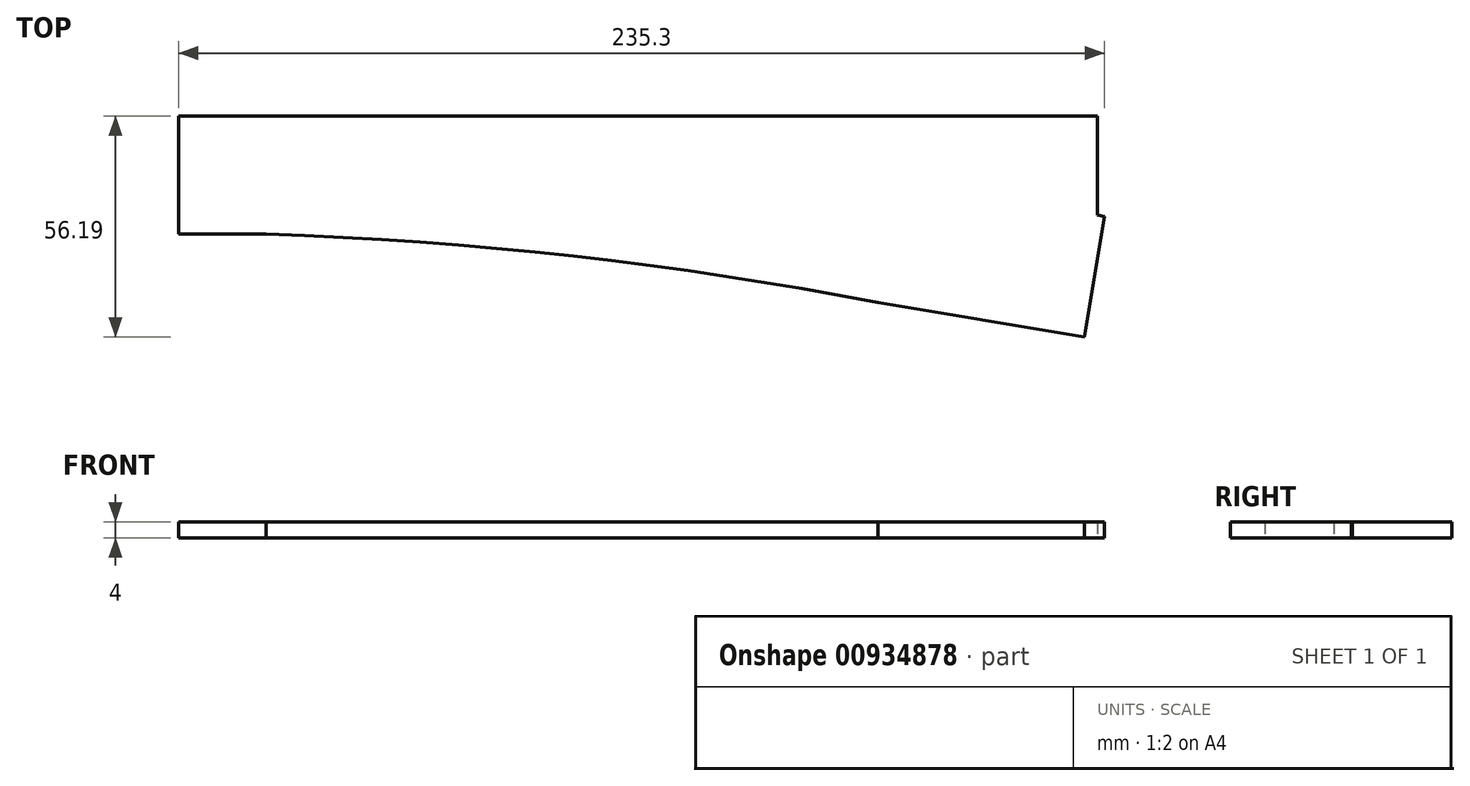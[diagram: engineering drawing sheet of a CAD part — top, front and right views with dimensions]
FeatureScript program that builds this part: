
annotation { "Feature Type Name" : "Feature", "Feature Type Description" : "" }
export const myFeature = defineFeature(function(context is Context, id is Id, definition is map)
    precondition{}
    {
        {
            var Q0;
            Q0=qCreatedBy(makeId("Top.planeOp"),FACE);
            var sketch = newSketch(context, id + "F0", { "sketchPlane" : qUnion([Q0])});
            skPoint(sketch, "E0.startSnap0", {"position": v(97.75, -3.18) * mm});
            skLineSegment(sketch, "E1.bottom", {"start": v(-138.74, -10.87) * mm, "end": v(94.76, -10.87) * mm});
            skLineSegment(sketch, "E1.top", {"start": v(-138.74, -40.87) * mm, "end": v(-116.46, -40.87) * mm});
            skLineSegment(sketch, "E1.left", {"start": v(-138.74, -10.87) * mm, "end": v(-138.74, -40.87) * mm});
            skLineSegment(sketch, "E1.right", {"start": v(94.76, -10.87) * mm, "end": v(94.76, -36.07) * mm});
            skLineSegment(sketch, "E2", {"start": v(-138.74, -25.87) * mm, "end": v(94.76, -25.87) * mm, "construction": true});
            skLineSegment(sketch, "E3", {"start": v(-138.74, -17.37) * mm, "end": v(94.76, -17.37) * mm, "construction": true});
            skLineSegment(sketch, "E4", {"start": v(-138.74, -34.37) * mm, "end": v(94.76, -34.37) * mm, "construction": true});
            skLineSegment(sketch, "E5", {"start": v(43.02, -34) * mm, "end": v(132.01, -48.9) * mm, "construction": true});
            skLineSegment(sketch, "E6", {"start": v(-116.46, -4.1) * mm, "end": v(-116.46, -86.5) * mm, "construction": true});
            skLineSegment(sketch, "E7", {"start": v(59.06, 61.83) * mm, "end": v(36.75, -71.5) * mm, "construction": true});
            skLineSegment(sketch, "E8", {"start": v(129.2, -65.66) * mm, "end": v(40.16, -50.76) * mm, "construction": true});
            skArc(sketch, "E9", {"start": v(41.64, -42.26) * mm, "mid": v(-37.11, -31.18) * mm, "end": v(-116.46, -25.87) * mm, "construction": true});
            skLineSegment(sketch, "E10", {"start": v(41.64, -42.26) * mm, "end": v(93.97, -51.57) * mm, "construction": true});
            skLineSegment(sketch, "E11", {"start": v(94.76, -36.07) * mm, "end": v(96.56, -36.37) * mm});
            skLineSegment(sketch, "E12", {"start": v(134.3, -35.2) * mm, "end": v(124.94, -91.15) * mm, "construction": true});
            skLineSegment(sketch, "E13", {"start": v(96.56, -36.37) * mm, "end": v(91.42, -67.06) * mm});
            skPoint(sketch, "E14.orphan", {"position": v(133.09, -42.48) * mm});
            skPoint(sketch, "E15.end.orphan", {"position": v(128.14, -72.07) * mm});
            skLineSegment(sketch, "E16", {"start": v(91.42, -67.06) * mm, "end": v(38.96, -58.28) * mm});
            skArc(sketch, "E17", {"start": v(38.96, -58.28) * mm, "mid": v(-38.4, -46.49) * mm, "end": v(-116.46, -40.87) * mm});
            skLineSegment(sketch, "E18.trimOffspring", {"start": v(33.68, -40.87) * mm, "end": v(94.76, -40.87) * mm});
            skArc(sketch, "E19", {"start": v(43.02, -34) * mm, "mid": v(-36.42, -22.79) * mm, "end": v(-116.46, -17.37) * mm, "construction": true});
            skSolve(sketch);
        }
        {
            var Q0;
            Q0=makeQuery(id+"F0.imprint","IMPRINT",FACE,{"disambiguationData":[TD([[makeQuery(id+"F0.imprint","IMPRINT",EDGE,{"derivedFrom":sQuery(id+"F0.wireOp",EDGE,"E1.bottom")}),-1.0]])]});
            extrude(context, id + "F1", {"entities" : qUnion([Q0]), "depth" : 4 * mm, "offsetDistance" : 25 * mm});
        }
        {
            var Q0;
            Q0=makeQuery(id+"F1.opExtrude","SWEPT_FACE",FACE,{"disambiguationData":[OSD([sQuery(id+"F0.wireOp",EDGE,"E1.left")])]});
            var sketch = newSketch(context, id + "F2", { "sketchPlane" : qUnion([Q0])});
            skLineSegment(sketch, "E20", {"start": v(17.37, 0) * mm, "end": v(18.38, 0) * mm});
            skLineSegment(sketch, "E21", {"start": v(17.37, 2.1) * mm, "end": v(17.75, 2.1) * mm});
            skLineSegment(sketch, "E22", {"start": v(18.38, 0) * mm, "end": v(18.38, 0.28) * mm});
            skLineSegment(sketch, "E23", {"start": v(18.3, 0.4) * mm, "end": v(17.58, 0.6) * mm});
            skPoint(sketch, "E24.visualSharp", {"position": v(17.88, 2.1) * mm});
            skArc(sketch, "E24.filletArc", {"start": v(17.88, 1.98) * mm, "mid": v(17.84, 2.07) * mm, "end": v(17.75, 2.1) * mm});
            skPoint(sketch, "E25.visualSharp", {"position": v(17.88, 1.6) * mm});
            skPoint(sketch, "E26.visualSharp", {"position": v(17.49, 0.62) * mm});
            skArc(sketch, "E26.filletArc", {"start": v(17.49, 0.72) * mm, "mid": v(17.52, 0.64) * mm, "end": v(17.58, 0.6) * mm});
            skPoint(sketch, "E27.visualSharp", {"position": v(18.38, 0.38) * mm});
            skArc(sketch, "E27.filletArc", {"start": v(18.38, 0.28) * mm, "mid": v(18.36, 0.36) * mm, "end": v(18.3, 0.4) * mm});
            skLineSegment(sketch, "E28.MirrorCS", {"start": v(17.37, 2.1) * mm, "end": v(16.99, 2.1) * mm});
            skArc(sketch, "E29.MirrorCS", {"start": v(27.32, -17.25) * mm, "mid": v(27.26, -17.29) * mm, "end": v(27.2, -17.33) * mm});
            skLineSegment(sketch, "E30.MirrorCS", {"start": v(16.45, 0.4) * mm, "end": v(17.15, 0.6) * mm});
            skPoint(sketch, "E31.MirrorP", {"position": v(16.35, 0.38) * mm});
            skLineSegment(sketch, "E32.MirrorCS", {"start": v(16.35, 0) * mm, "end": v(16.35, 0.28) * mm});
            skLineSegment(sketch, "E33.MirrorCS", {"start": v(17.37, 0) * mm, "end": v(16.35, 0) * mm});
            skLineSegment(sketch, "E34", {"start": v(17.88, 1.98) * mm, "end": v(17.88, 1.7) * mm});
            skLineSegment(sketch, "E35", {"start": v(17.79, 1.57) * mm, "end": v(17.58, 1.51) * mm});
            skLineSegment(sketch, "E36", {"start": v(17.49, 0.72) * mm, "end": v(17.49, 1.4) * mm});
            skArc(sketch, "E37.filletArc", {"start": v(17.79, 1.57) * mm, "mid": v(17.85, 1.62) * mm, "end": v(17.88, 1.7) * mm});
            skPoint(sketch, "E38.visualSharp", {"position": v(17.49, 1.49) * mm});
            skArc(sketch, "E38.filletArc", {"start": v(17.58, 1.51) * mm, "mid": v(17.51, 1.47) * mm, "end": v(17.49, 1.4) * mm});
            skLineSegment(sketch, "E39.MirrorCS", {"start": v(16.95, 1.57) * mm, "end": v(17.16, 1.51) * mm});
            skArc(sketch, "E40.MirrorCS", {"start": v(27, -16.35) * mm, "mid": v(26.99, -16.35) * mm, "end": v(26.98, -16.36) * mm});
            skLineSegment(sketch, "E41.MirrorCS", {"start": v(17.25, 0.72) * mm, "end": v(17.25, 1.4) * mm});
            skLineSegment(sketch, "E42.MirrorCS", {"start": v(16.86, 1.98) * mm, "end": v(16.86, 1.7) * mm});
            skLineSegment(sketch, "E43", {"start": v(17.37, 0) * mm, "end": v(17.37, 2.1) * mm, "construction": true});
            skArc(sketch, "E44.MirrorCS", {"start": v(16.86, 1.98) * mm, "mid": v(16.9, 2.07) * mm, "end": v(16.99, 2.1) * mm});
            skArc(sketch, "E45.MirrorCS", {"start": v(16.95, 1.57) * mm, "mid": v(16.89, 1.62) * mm, "end": v(16.86, 1.7) * mm});
            skArc(sketch, "E46.MirrorCS", {"start": v(17.16, 1.51) * mm, "mid": v(17.22, 1.47) * mm, "end": v(17.25, 1.4) * mm});
            skArc(sketch, "E47.MirrorCS", {"start": v(17.25, 0.72) * mm, "mid": v(17.22, 0.64) * mm, "end": v(17.15, 0.6) * mm});
            skArc(sketch, "E48.MirrorCS", {"start": v(16.35, 0.28) * mm, "mid": v(16.38, 0.36) * mm, "end": v(16.45, 0.4) * mm});
            skSolve(sketch);
        }
    });
